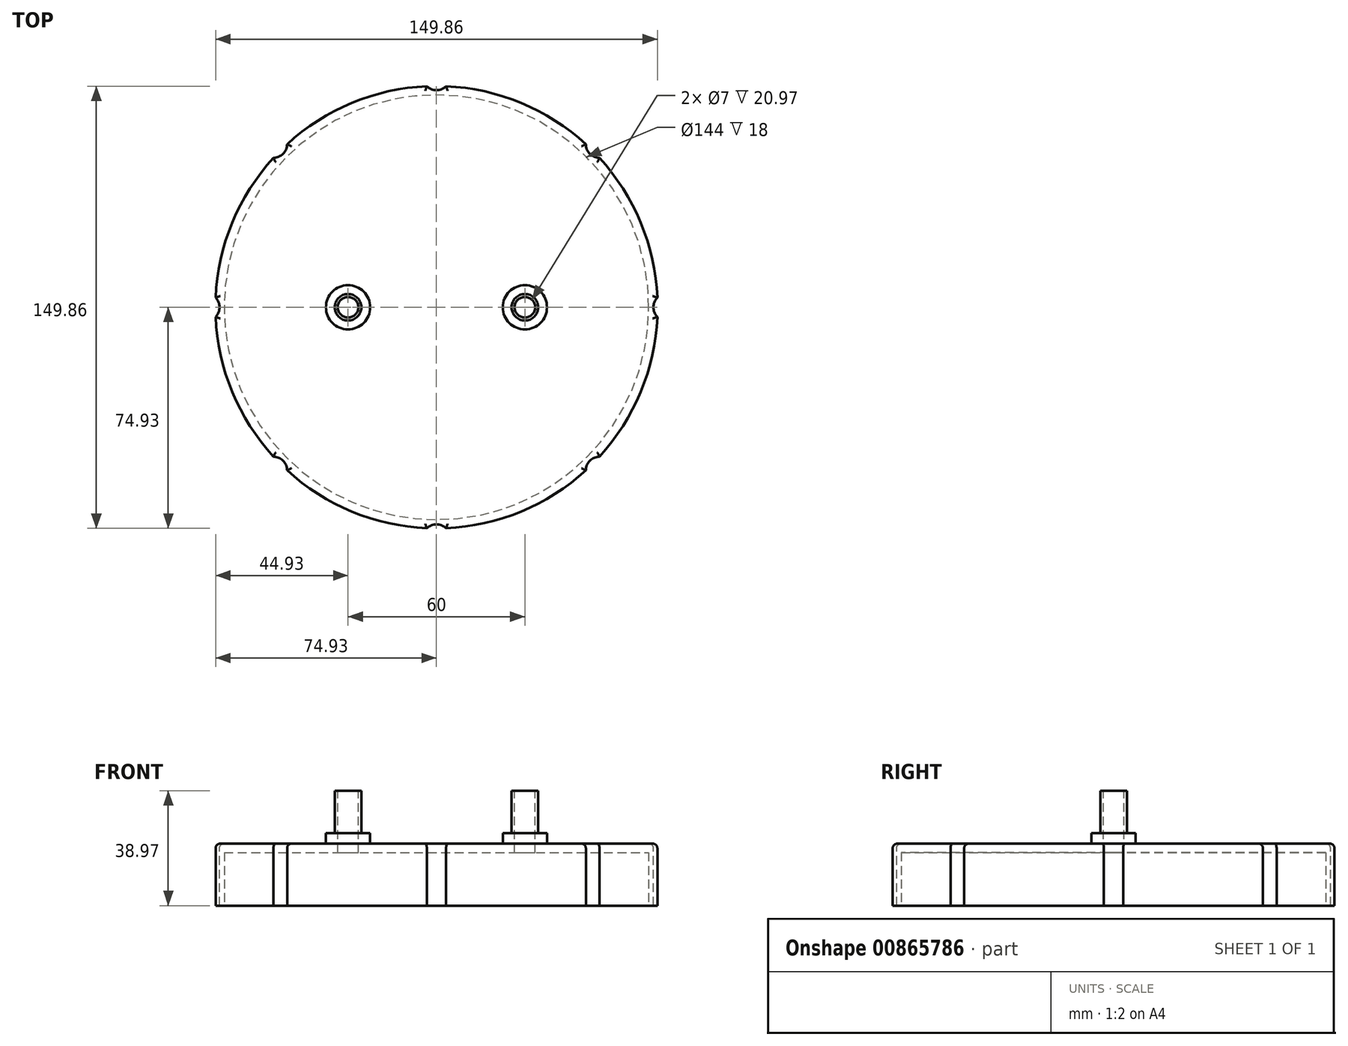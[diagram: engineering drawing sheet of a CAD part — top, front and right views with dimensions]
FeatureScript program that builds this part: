
annotation { "Feature Type Name" : "Feature", "Feature Type Description" : "" }
export const myFeature = defineFeature(function(context is Context, id is Id, definition is map)
    precondition{}
    {
        {
            var Q0;
            Q0=qCreatedBy(makeId("Top.planeOp"),FACE);
            var sketch = newSketch(context, id + "F0", { "sketchPlane" : qUnion([Q0])});
            skCircle(sketch, "E0", {"center": v(0, 0) * mm, "radius": 75 * mm});
            skSolve(sketch);
        }
        {
            var Q0;
            Q0 = qSketchRegion(id + "F0", true);
            extrude(context, id + "F1", {"entities" : qUnion([Q0]), "depth" : 21 * mm, "offsetDistance" : 25 * mm});
        }
        {
            var Q0;
            Q0=makeQuery(id+"F1.opExtrude","CAP_FACE",FACE,{"disambiguationData":[OSD([sQuery(id+"F0.wireOp",EDGE,"E0")])],"isStart":false});
            var sketch = newSketch(context, id + "F2", { "sketchPlane" : qUnion([Q0])});
            skCircle(sketch, "E1", {"center": v(0, 78.26) * mm, "radius": 4.67 * mm});
            skCircle(sketch, "E2.1.0", {"center": v(-55.34, 55.34) * mm, "radius": 4.67 * mm});
            skCircle(sketch, "E2.2.0", {"center": v(-78.26, 0) * mm, "radius": 4.67 * mm});
            skCircle(sketch, "E2.3.0", {"center": v(-55.34, -55.34) * mm, "radius": 4.67 * mm});
            skCircle(sketch, "E2.4.0", {"center": v(0, -78.26) * mm, "radius": 4.67 * mm});
            skCircle(sketch, "E2.5.0", {"center": v(55.34, -55.34) * mm, "radius": 4.67 * mm});
            skCircle(sketch, "E2.6.0", {"center": v(78.26, 0) * mm, "radius": 4.67 * mm});
            skCircle(sketch, "E2.7.0", {"center": v(55.34, 55.34) * mm, "radius": 4.67 * mm});
            skPoint(sketch, "E2.center", {"position": v(0, 0) * mm});
            skSolve(sketch);
        }
        {
            var Q0;
            Q0 = qSketchRegion(id + "F2", true);
            extrude(context, id + "F3", {"entities" : qUnion([Q0]), "operationType" : NewBodyOperationType.REMOVE, "endBound" : BoundingType.THROUGH_ALL, "oppositeDirection" : true, "depth" : 25 * mm, "offsetDistance" : 25 * mm});
        }
        {
            var Q0;
            Q0=makeQuery(id+"F1.opExtrude","CAP_FACE",FACE,{"disambiguationData":[OSD([sQuery(id+"F0.wireOp",EDGE,"E0")])],"isStart":false});
            fillet(context, id + "F4", {"entities" : qUnion([Q0]), "radius" : 1.5 * mm, "tangentPropagation" : true, "allowEdgeOverflow" : false});
        }
        {
            var Q0;
            Q0=makeQuery(id+"F1.opExtrude","CAP_FACE",FACE,{"disambiguationData":[OSD([sQuery(id+"F0.wireOp",EDGE,"E0")])],"isStart":false});
            var sketch = newSketch(context, id + "F5", { "sketchPlane" : qUnion([Q0])});
            skCircle(sketch, "E3", {"center": v(-30, 0) * mm, "radius": 7.5 * mm});
            skCircle(sketch, "E4.MirrorC", {"center": v(30, 0) * mm, "radius": 7.5 * mm});
            skSolve(sketch);
        }
        {
            var Q0;
            Q0 = qSketchRegion(id + "F5", true);
            extrude(context, id + "F6", {"entities" : qUnion([Q0]), "operationType" : NewBodyOperationType.ADD, "depth" : 3.57 * mm, "offsetDistance" : 25 * mm});
        }
        {
            var Q0;
            Q0=makeQuery(id+"F6.opExtrude","CAP_FACE",FACE,{"disambiguationData":[OSD([sQuery(id+"F5.wireOp",EDGE,"E3")])],"isStart":false});
            var sketch = newSketch(context, id + "F7", { "sketchPlane" : qUnion([Q0])});
            skCircle(sketch, "E5", {"center": v(-30, 0) * mm, "radius": 4.5 * mm});
            skCircle(sketch, "E6.0", {"center": v(30, 0) * mm, "radius": 7.5 * mm});
            skCircle(sketch, "E7", {"center": v(30, 0) * mm, "radius": 4.5 * mm});
            skSolve(sketch);
        }
        {
            var Q0;
            Q0=makeQuery(id+"F7.imprint","IMPRINT",FACE,{"disambiguationData":[TD([[makeQuery(id+"F7.imprint","IMPRINT",EDGE,{"derivedFrom":sQuery(id+"F7.wireOp",EDGE,"E5")}),1.0]])]});
            var Q1;
            Q1=makeQuery(id+"F7.imprint","IMPRINT",FACE,{"disambiguationData":[TD([[makeQuery(id+"F7.imprint","IMPRINT",EDGE,{"derivedFrom":sQuery(id+"F7.wireOp",EDGE,"E7")}),1.0]])]});
            extrude(context, id + "F8", {"entities" : qUnion([Q0, Q1]), "operationType" : NewBodyOperationType.ADD, "depth" : 14.4 * mm, "offsetDistance" : 25 * mm});
        }
        {
            var Q0;
            Q0=makeQuery(id+"F1.opExtrude","CAP_FACE",FACE,{"disambiguationData":[OSD([sQuery(id+"F0.wireOp",EDGE,"E0")])],"isStart":true});
            var sketch = newSketch(context, id + "F9", { "sketchPlane" : qUnion([Q0])});
            skCircle(sketch, "E8", {"center": v(0, 0) * mm, "radius": 72 * mm});
            skSolve(sketch);
        }
        {
            var Q0;
            Q0 = qSketchRegion(id + "F9", true);
            extrude(context, id + "F10", {"entities" : qUnion([Q0]), "operationType" : NewBodyOperationType.REMOVE, "oppositeDirection" : true, "depth" : 18 * mm, "offsetDistance" : 25 * mm});
        }
        {
            var Q0;
            Q0=makeQuery(id+"F8.opExtrude","CAP_FACE",FACE,{"disambiguationData":[OSD([sQuery(id+"F7.wireOp",EDGE,"E5")])],"isStart":false});
            var sketch = newSketch(context, id + "F11", { "sketchPlane" : qUnion([Q0])});
            skCircle(sketch, "E9", {"center": v(-30, 0) * mm, "radius": 3.5 * mm});
            skCircle(sketch, "E10.0", {"center": v(30, 0) * mm, "radius": 4.5 * mm});
            skCircle(sketch, "E11", {"center": v(30, 0) * mm, "radius": 3.5 * mm});
            skSolve(sketch);
        }
        {
            var Q0;
            Q0=makeQuery(id+"F11.imprint","IMPRINT",FACE,{"disambiguationData":[TD([[makeQuery(id+"F11.imprint","IMPRINT",EDGE,{"derivedFrom":sQuery(id+"F11.wireOp",EDGE,"E11")}),1.0]])]});
            var Q1;
            Q1=makeQuery(id+"F11.imprint","IMPRINT",FACE,{"disambiguationData":[TD([[makeQuery(id+"F11.imprint","IMPRINT",EDGE,{"derivedFrom":sQuery(id+"F11.wireOp",EDGE,"E9")}),1.0]])]});
            extrude(context, id + "F12", {"entities" : qUnion([Q0, Q1]), "operationType" : NewBodyOperationType.REMOVE, "endBound" : BoundingType.THROUGH_ALL, "oppositeDirection" : true, "depth" : 25 * mm, "offsetDistance" : 25 * mm});
        }
    });
